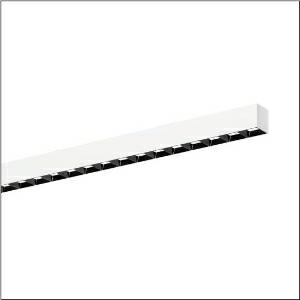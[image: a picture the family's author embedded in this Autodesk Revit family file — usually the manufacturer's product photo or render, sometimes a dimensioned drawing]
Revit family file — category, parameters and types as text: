
# Revit family: silica_r__21_51mx22da34wb_da43
name_source: partatom
category: Lighting Fixtures
units: mm (PartAtom-declared; Revit-internal decimal feet)

## family parameters
Cut with Voids When Loaded = No
Host = Face
Light Source = No
Part Type = Normal
Room Calculation Point = No
Round Connector Dimension = Use Diameter
Shared = No

## types (1)
- --- (1 x LED, 4320 lm, 27.4 W, 3000K)
    Apparent Load = 27 VA
    CIE Flux Codes = 86 100 100 100 100
    Color Rendering = 80
    Color Temperature = 3000K
    Default Elevation = 1800 mm
    Description = Silica® 21, office luminaire, primary light control with darklight reflector, of PMMA, black, CAT 2 (L<= 3000cd/m²), light emission: direct distribution, primary light characteristic: symmetric, installation type: surface-mounted, LED, rated luminous flux: 4.320lm, luminous efficacy: 158lm/W, light colour: 830, colour temperature: 3000K, control gear: DALI 2, with terminal, 3+2-pole, max. 2.5mm², mains connection: 220..240V, AC, 50/60Hz, rated input power: 27.4W, luminaire housing, of aluminium, traffic white (RAL 9016), length: 1.204mm, width: 53mm, height: 53mm, protection rating (complete): IP20, insulation class (complete): insulation class I (protective earthing), certification: CE, permissible operating ambient temperature: 0..+35°C, standard: EN 50419, packaging unit: 1 piece
    Height = 53 mm
    Lamp = 1 x LED
    Lamp Light Flux = 4320 lm
    Lamp Power = 27.4 W
    Lamp count = 1
    Length = 1204 mm
    Luminous efficacy = 158 lm/W
    Manufacturer = Siteco
    ModVariant = No
    Model = 51MX22DA34WB
    Mounting Place = Ceiling
    Mounting Type = Surface mounted
    Number of Poles = 1
    OnlyDefault = Yes
    Power Factor = 1
    Product Name = Silica® 21
    Product group = office luminaire | ceiling mounted
    ProductGroupID = 302
    Protection Class = Protection class I
    Protection Degree = IP 20
    RLX_Detail_Level = 1
    RLX_Emergency_Light_Flux = 0 lm
    RLX_Emergency_Type = 0
    RLX_Emergency_Type_DB = No
    RlxData = <blob elided: 41121 chars, md5=585f8610>
    Socket = socket
    Standby Power = 0 W
    System Light Flux = 4320 lm
    System Power = 27 W
    Type Comments = factory setting: luminous flux: 100 % | dim-lin: 254 | 392 mA
    Type Image = l_1335873.jpg
    URL = http://relux.com
    VarID = @adj_008835
    Voltage = 0 V
    Weight = 0.00 kg
    Width = 53 mm

## geometry (parser evidence)
native form markers: Blend x4, Sweep x11
no freeform markers — native parametric forms only
